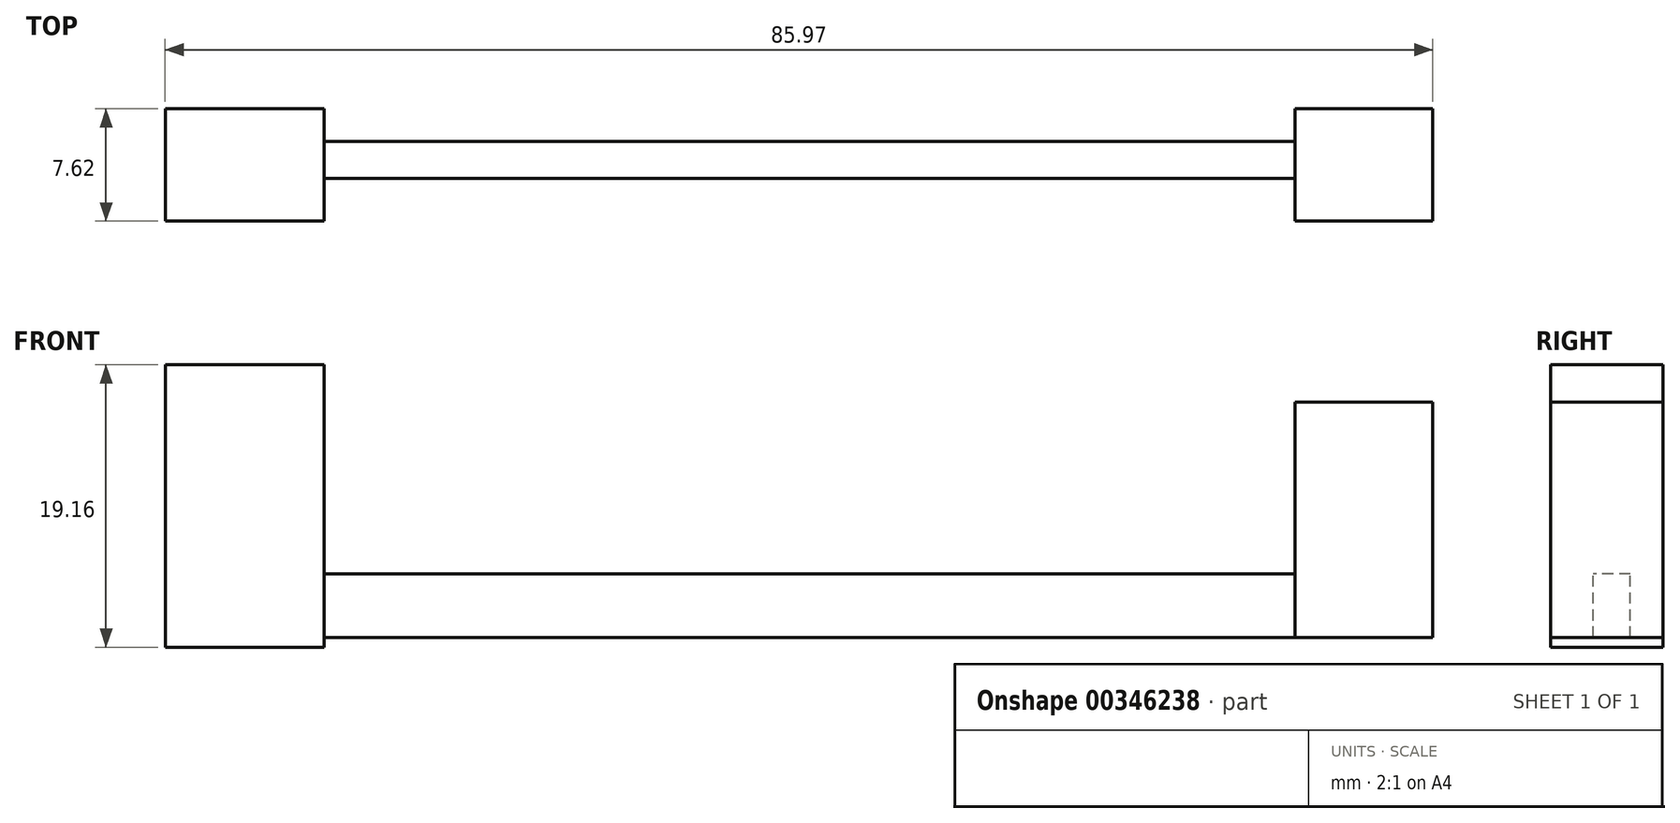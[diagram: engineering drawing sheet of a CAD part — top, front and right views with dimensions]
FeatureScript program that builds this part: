
annotation { "Feature Type Name" : "Feature", "Feature Type Description" : "" }
export const myFeature = defineFeature(function(context is Context, id is Id, definition is map)
    precondition{}
    {
        {
            var Q0;
            Q0=qCreatedBy(makeId("Front.planeOp"),FACE);
            var sketch = newSketch(context, id + "F0", { "sketchPlane" : qUnion([Q0])});
            skLineSegment(sketch, "E0.bottom", {"start": v(-9.33, 37.8) * mm, "end": v(0, 37.8) * mm});
            skLineSegment(sketch, "E0.top", {"start": v(-9.33, 21.83) * mm, "end": v(0, 21.83) * mm});
            skLineSegment(sketch, "E0.left", {"start": v(-9.33, 37.8) * mm, "end": v(-9.33, 21.83) * mm});
            skLineSegment(sketch, "E0.right", {"start": v(0, 37.8) * mm, "end": v(0, 21.83) * mm});
            skSolve(sketch);
        }
        {
            var Q0;
            Q0=makeQuery(id+"F0.imprint","IMPRINT",FACE,{"disambiguationData":[TD([[makeQuery(id+"F0.imprint","IMPRINT",EDGE,{"derivedFrom":sQuery(id+"F0.wireOp",EDGE,"E0.bottom")}),-1.0]])]});
            extrude(context, id + "F1", {"entities" : qUnion([Q0]), "depth" : 7.62 * mm});
        }
        {
            var Q0;
            Q0=makeQuery(id+"F1.opExtrude","SWEPT_FACE",FACE,{"disambiguationData":[OSD([sQuery(id+"F0.wireOp",EDGE,"E0.left")])]});
            var sketch = newSketch(context, id + "F2", { "sketchPlane" : qUnion([Q0])});
            skLineSegment(sketch, "E1.bottom", {"start": v(2.22, 21.83) * mm, "end": v(4.72, 21.83) * mm});
            skLineSegment(sketch, "E1.top", {"start": v(2.22, 26.14) * mm, "end": v(4.72, 26.14) * mm});
            skLineSegment(sketch, "E1.left", {"start": v(2.22, 21.83) * mm, "end": v(2.22, 26.14) * mm});
            skLineSegment(sketch, "E1.right", {"start": v(4.72, 21.83) * mm, "end": v(4.72, 26.14) * mm});
            skSolve(sketch);
        }
        {
            var Q0;
            Q0=makeQuery(id+"F2.imprint","IMPRINT",FACE,{"disambiguationData":[TD([[makeQuery(id+"F2.imprint","IMPRINT",EDGE,{"derivedFrom":sQuery(id+"F2.wireOp",EDGE,"E1.bottom")}),-1.0]])]});
            extrude(context, id + "F3", {"entities" : qUnion([Q0]), "operationType" : NewBodyOperationType.ADD, "depth" : 25.4 * mm});
        }
        {
            var Q0;
            Q0=makeQuery(id+"F3.opExtrude","CAP_FACE",FACE,{"disambiguationData":[OSD([sQuery(id+"F2.wireOp",EDGE,"E1.bottom"),sQuery(id+"F2.wireOp",EDGE,"E1.top"),sQuery(id+"F2.wireOp",EDGE,"E1.left"),sQuery(id+"F2.wireOp",EDGE,"E1.right")])],"isStart":false});
            extrude(context, id + "F4", {"entities" : qUnion([Q0]), "operationType" : NewBodyOperationType.ADD, "depth" : 25.4 * mm});
        }
        {
            var Q0;
            Q0=makeQuery(id+"F4.opExtrude","CAP_FACE",FACE,{"disambiguationData":[OSD([sQuery(id+"F2.wireOp",EDGE,"E1.bottom"),sQuery(id+"F2.wireOp",EDGE,"E1.top"),sQuery(id+"F2.wireOp",EDGE,"E1.left"),sQuery(id+"F2.wireOp",EDGE,"E1.right")])],"isStart":false});
            extrude(context, id + "F5", {"entities" : qUnion([Q0]), "operationType" : NewBodyOperationType.ADD, "depth" : 25.4 * mm});
        }
        {
            var Q0;
            Q0=qCreatedBy(makeId("Front.planeOp"),FACE);
            var sketch = newSketch(context, id + "F6", { "sketchPlane" : qUnion([Q0])});
            skLineSegment(sketch, "E2.bottom", {"start": v(-75.2, 21.16) * mm, "end": v(-85.97, 21.16) * mm});
            skLineSegment(sketch, "E2.top", {"start": v(-75.2, 40.32) * mm, "end": v(-85.97, 40.32) * mm});
            skLineSegment(sketch, "E2.left", {"start": v(-75.2, 21.16) * mm, "end": v(-75.2, 40.32) * mm});
            skLineSegment(sketch, "E2.right", {"start": v(-85.97, 21.16) * mm, "end": v(-85.97, 40.32) * mm});
            skSolve(sketch);
        }
        {
            var Q0;
            Q0=makeQuery(id+"F6.imprint","IMPRINT",FACE,{"disambiguationData":[TD([[makeQuery(id+"F6.imprint","IMPRINT",EDGE,{"derivedFrom":sQuery(id+"F6.wireOp",EDGE,"E2.bottom")}),-1.0]])]});
            extrude(context, id + "F7", {"entities" : qUnion([Q0]), "operationType" : NewBodyOperationType.ADD, "depth" : 7.62 * mm});
        }
    });
